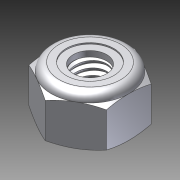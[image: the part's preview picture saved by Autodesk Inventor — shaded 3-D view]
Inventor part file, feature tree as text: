
AUTODESK INVENTOR PART (.ipt)
format: ipt  version: 2014 SP1 (Build 180222100, 222)  size: 335,872 bytes
history: native  units: in
note: dims shown in document units (in); Inventor stores cm internally (conversion verified against a paired STEP export)
features: other x2, imported_body x2, revolve x1
ambient origin geometry x8: Origin, YZ Plane, XZ Plane, XY Plane, X Axis, Y Axis, Z Axis, Center Point
bodies: Body1 (feature_tree), Body2 (feature_tree)
feature tree (5):
  other  "Cut-Revolve4"
  other  "10-32 Nylock Nut 1_90631A411.ipt1"
  revolve  "Revolve2"  [1 undecoded]
  imported_body  "Base1"
  imported_body  "Base2"
note: 1 required parameter value undecoded (feature->parameter linkage not recoverable at this tier; creation-order binding heuristic only, values carry confidence <= 0.55)
